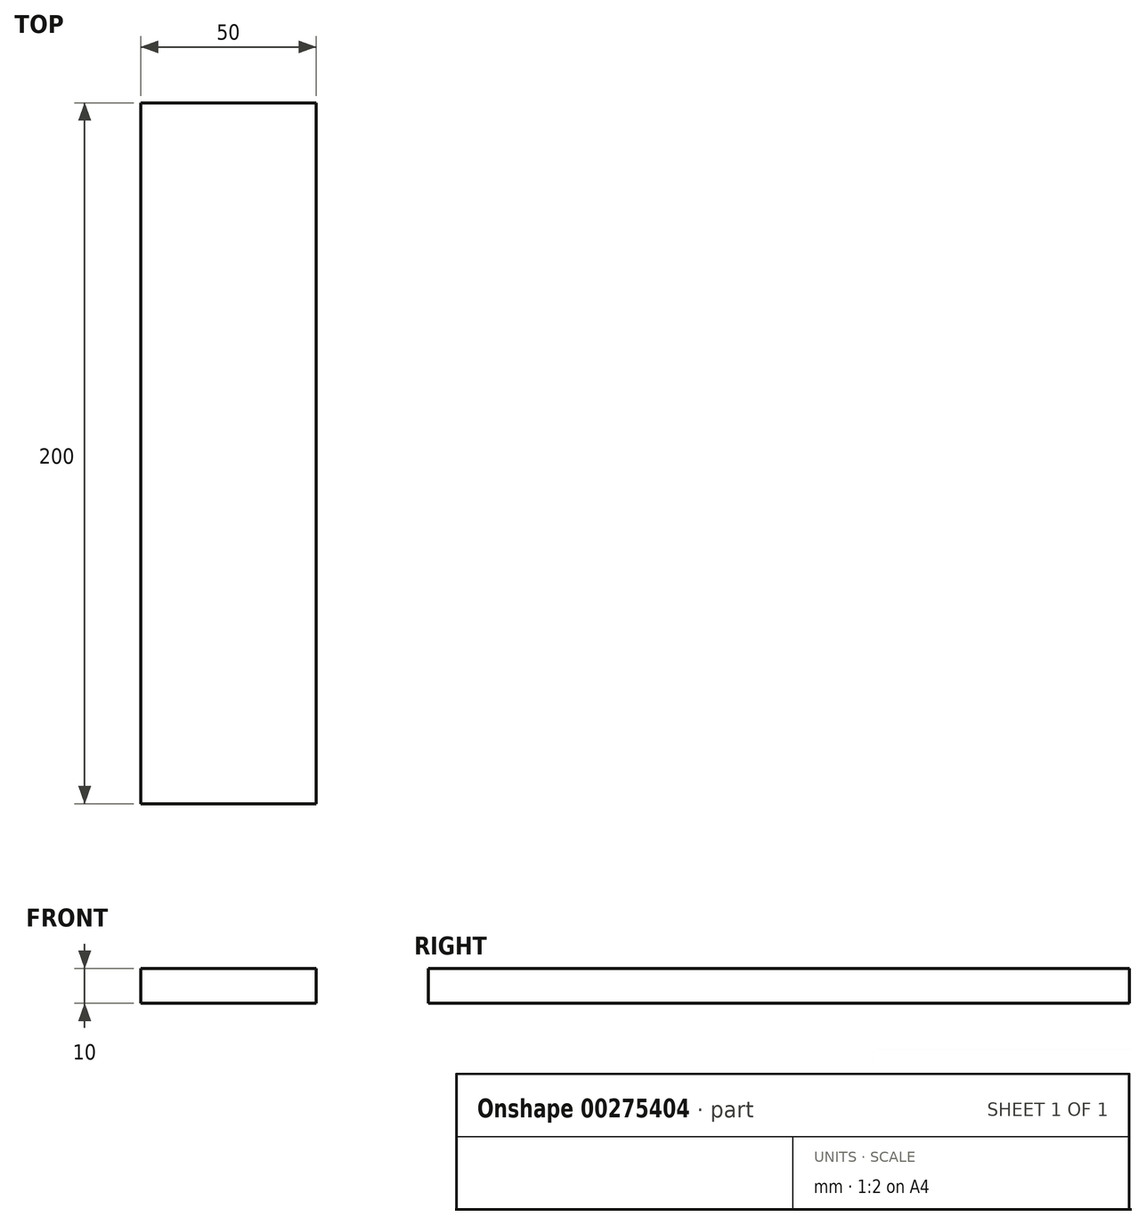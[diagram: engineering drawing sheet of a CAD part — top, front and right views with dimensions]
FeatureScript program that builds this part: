
annotation { "Feature Type Name" : "Feature", "Feature Type Description" : "" }
export const myFeature = defineFeature(function(context is Context, id is Id, definition is map)
    precondition{}
    {
        {
            var Q0;
            Q0=qCreatedBy(makeId("Front.planeOp"),FACE);
            var sketch = newSketch(context, id + "F0", { "sketchPlane" : qUnion([Q0])});
            skLineSegment(sketch, "E0.bottom", {"start": v(-30, 5) * mm, "end": v(20, 5) * mm});
            skLineSegment(sketch, "E0.top", {"start": v(-30, -5) * mm, "end": v(20, -5) * mm});
            skLineSegment(sketch, "E0.left", {"start": v(-30, 5) * mm, "end": v(-30, -5) * mm});
            skLineSegment(sketch, "E0.right", {"start": v(20, 5) * mm, "end": v(20, -5) * mm});
            skSolve(sketch);
        }
        {
            var Q0;
            Q0 = qSketchRegion(id + "F0", true);
            extrude(context, id + "F1", {"entities" : qUnion([Q0]), "depth" : 200 * mm});
        }
    });
